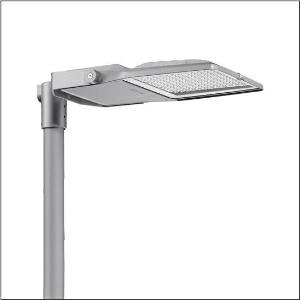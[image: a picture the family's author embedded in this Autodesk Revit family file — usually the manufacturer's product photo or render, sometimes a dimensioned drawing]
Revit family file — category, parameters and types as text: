
# Revit family: floodlight_fl_21_iq_midi___pl52_5xa7782f2d3a_028a
name_source: partatom
category: Lighting Fixtures
units: mm (PartAtom-declared; Revit-internal decimal feet)

## family parameters
Cut with Voids When Loaded = No
Host = Face
Light Source = No
Part Type = Normal
Room Calculation Point = No
Round Connector Dimension = Use Diameter
Shared = No

## types (1)
- --- (1 x LED, 35760 lm, 270.2 W, 3000K)
    Apparent Load = 270 VA
    CIE Flux Codes = 26 60 98 100 100
    Color Rendering = 70
    Color Temperature = 3000K
    Default Elevation = 1800 mm
    Description = Floodlight FL 21 iQ midi, floodlight, primary light control with lens, of PMMA, primary optical cover: protective disc, of toughened safety glass, transparent, light distribution: PL52, light emission: direct distribution, installation type: surface-mounted, LED, High Power LED, rated luminous flux: 35.760lm, luminous efficacy: 132lm/W, light colour: 730, colour temperature: 3000K, control gear: ECG iQ, control: optimised constant luminous flux control (CLO 2.0), Desk-Remote (wireless, voltage-free reading and setting of iQ features in the workshop via application-optimized NFC function/RFID function), Smart-Wire, Night-Set, Temp-Guard, Auto-Match, Street-Remote, with terminal, 6-pole, mains connection: 220..240V, AC, 50/60Hz, start of lifetime: 270W, end of service life: 287W, reduction: 117W, luminaire housing, of diecast aluminium, powder-coated, Siteco® metallic grey (DB 702S), corrosivity category C5 mid according to DIN EN ISO 12944, sealing non-destructively replaceable, please order mast flange separately, mast bracket, of steel, galvanised, powder-coated, Siteco® metallic grey (DB 702S), protection rating (complete): IP66, insulation class (complete): insulation class II (safety insulation), certification: CE, protection symbol: D, impact resistance: IK08, permissible operating ambient temperature: -40..+40°C, permissible operating ambient temperature for outdoor applications: -40..+50°C, standard: DIN EN 12944, LABS conformity tested according to VDMA 24364:2018-05, packaging unit: 1 piece

Light Distribution: PL52
    Height = 76 mm
    Lamp = 1 x LED
    Lamp Light Flux = 35760 lm
    Lamp Power = 270.2 W
    Lamp count = 1
    Length = 657 mm
    Luminous efficacy = 132 lm/W
    Manufacturer = Siteco
    ModVariant = No
    Model = 5XA7782F2D3A
    Number of Poles = 1
    OnlyDefault = Yes
    Power Factor = 1
    Product Name = Floodlight FL 21 iQ midi | PL52
    Product group = floodlight | pylon annexe
    ProductGroupID = 6200
    Protection Class = Protection class II
    Protection Degree = IP 66
    RLX_Detail_Level = 1
    RLX_Emergency_Light_Flux = 0 lm
    RLX_Emergency_Type = 0
    RLX_Emergency_Type_DB = No
    RlxData = <blob elided: 153805 chars, md5=acd9d899>
    Socket = socket
    Standby Power = 0 W
    System Light Flux = 35760 lm
    System Power = 270 W
    Type Comments = factory setting: luminous flux: 100 % | dim-lin: 254 | 620 mA
    Type Image = l_1007123.jpg
    URL = http://relux.com
    VarID = @adj_035763
    Voltage = 0 V
    Weight = 0.00 kg
    Width = 442 mm

## geometry (parser evidence)
native form markers: Blend x4, Sweep x16
no freeform markers — native parametric forms only
